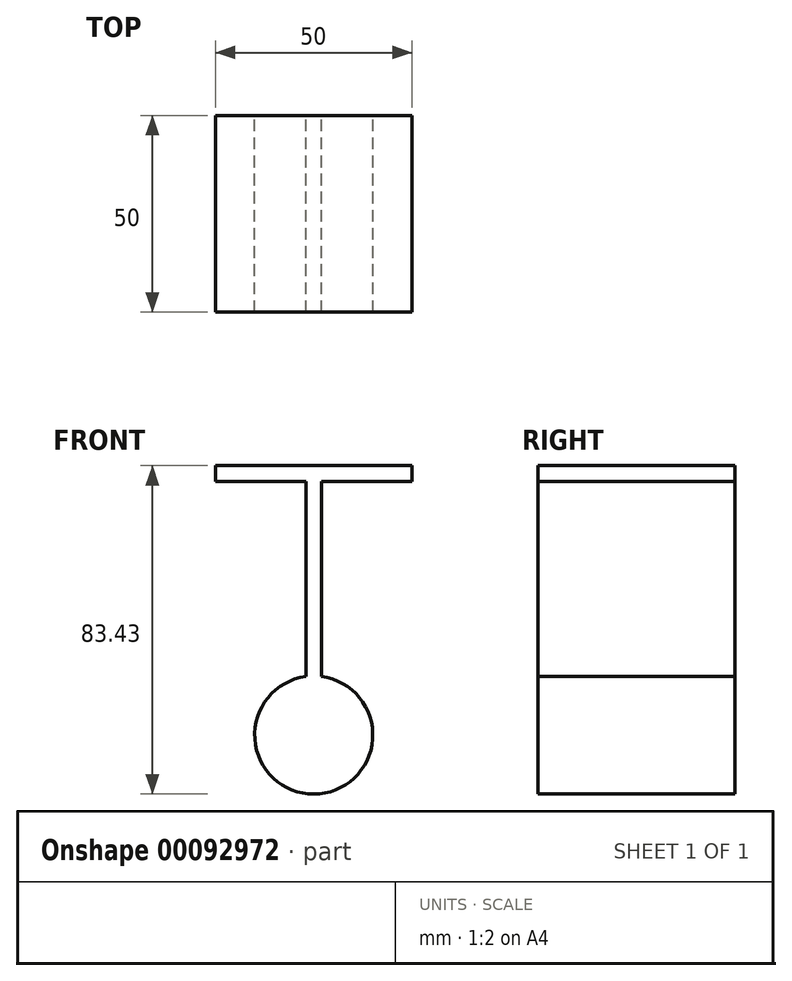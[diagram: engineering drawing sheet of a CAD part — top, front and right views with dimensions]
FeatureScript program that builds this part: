
annotation { "Feature Type Name" : "Feature", "Feature Type Description" : "" }
export const myFeature = defineFeature(function(context is Context, id is Id, definition is map)
    precondition{}
    {
        {
            var Q0;
            Q0=qCreatedBy(makeId("Front.planeOp"),FACE);
            var sketch = newSketch(context, id + "F0", { "sketchPlane" : qUnion([Q0])});
            skLineSegment(sketch, "E0.bottom", {"start": v(-2, 0) * mm, "end": v(2, 0) * mm});
            skLineSegment(sketch, "E0.top", {"start": v(-2, -50) * mm, "end": v(2, -50) * mm});
            skLineSegment(sketch, "E0.left", {"start": v(-2, 0) * mm, "end": v(-2, -50) * mm});
            skLineSegment(sketch, "E0.right", {"start": v(2, 0) * mm, "end": v(2, -50) * mm});
            skSolve(sketch);
        }
        {
            var Q0;
            Q0=makeQuery(id+"F0.imprint","IMPRINT",FACE,{"disambiguationData":[TD([[makeQuery(id+"F0.imprint","IMPRINT",EDGE,{"derivedFrom":sQuery(id+"F0.wireOp",EDGE,"E0.bottom")}),-1.0]])]});
            extrude(context, id + "F1", {"entities" : qUnion([Q0]), "endBound" : BoundingType.SYMMETRIC, "depth" : 50 * mm});
        }
        {
            var Q0;
            Q0=qCreatedBy(makeId("Front.planeOp"),FACE);
            var sketch = newSketch(context, id + "F2", { "sketchPlane" : qUnion([Q0])});
            skLineSegment(sketch, "E1.bottom", {"start": v(-25, 4) * mm, "end": v(25, 4) * mm});
            skLineSegment(sketch, "E1.top", {"start": v(-25, 0) * mm, "end": v(25, 0) * mm});
            skLineSegment(sketch, "E1.left", {"start": v(-25, 4) * mm, "end": v(-25, 0) * mm});
            skLineSegment(sketch, "E1.right", {"start": v(25, 4) * mm, "end": v(25, 0) * mm});
            skSolve(sketch);
        }
        {
            var Q0;
            Q0=makeQuery(id+"F2.imprint","IMPRINT",FACE,{"disambiguationData":[TD([[makeQuery(id+"F2.imprint","IMPRINT",EDGE,{"derivedFrom":sQuery(id+"F2.wireOp",EDGE,"E1.bottom")}),-1.0]])]});
            extrude(context, id + "F3", {"entities" : qUnion([Q0]), "operationType" : NewBodyOperationType.ADD, "endBound" : BoundingType.SYMMETRIC, "depth" : 50 * mm});
        }
        {
            var Q0;
            Q0=qCreatedBy(makeId("Front.planeOp"),FACE);
            var sketch = newSketch(context, id + "F4", { "sketchPlane" : qUnion([Q0])});
            skCircle(sketch, "E2", {"center": v(0, -64.43) * mm, "radius": 15 * mm});
            skSolve(sketch);
        }
        {
            var Q0;
            Q0=makeQuery(id+"F4.imprint","IMPRINT",FACE,{"disambiguationData":[TD([[makeQuery(id+"F4.imprint","IMPRINT",EDGE,{"derivedFrom":sQuery(id+"F4.wireOp",EDGE,"E2")}),1.0]])]});
            extrude(context, id + "F5", {"entities" : qUnion([Q0]), "operationType" : NewBodyOperationType.ADD, "endBound" : BoundingType.SYMMETRIC, "depth" : 50 * mm});
        }
    });
